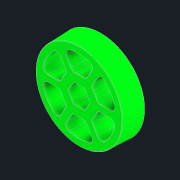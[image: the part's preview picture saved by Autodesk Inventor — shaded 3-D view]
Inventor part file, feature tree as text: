
AUTODESK INVENTOR PART (.ipt)
format: ipt  version: 2021 (Build 250183000, 183)  size: 739,328 bytes
history: native  units: in
note: dims shown in document units (in); Inventor stores cm internally (conversion verified against a paired STEP export)
features: fillet x1
ambient origin geometry x8: Origin, YZ Plane, XZ Plane, XY Plane, X Axis, Y Axis, Z Axis, Center Point
bodies: Solid1 (feature_tree)
feature tree (1):
  fillet  "Fillet3"  [1 undecoded]
note: 1 required parameter value undecoded (feature->parameter linkage not recoverable at this tier; creation-order binding heuristic only, values carry confidence <= 0.55)
